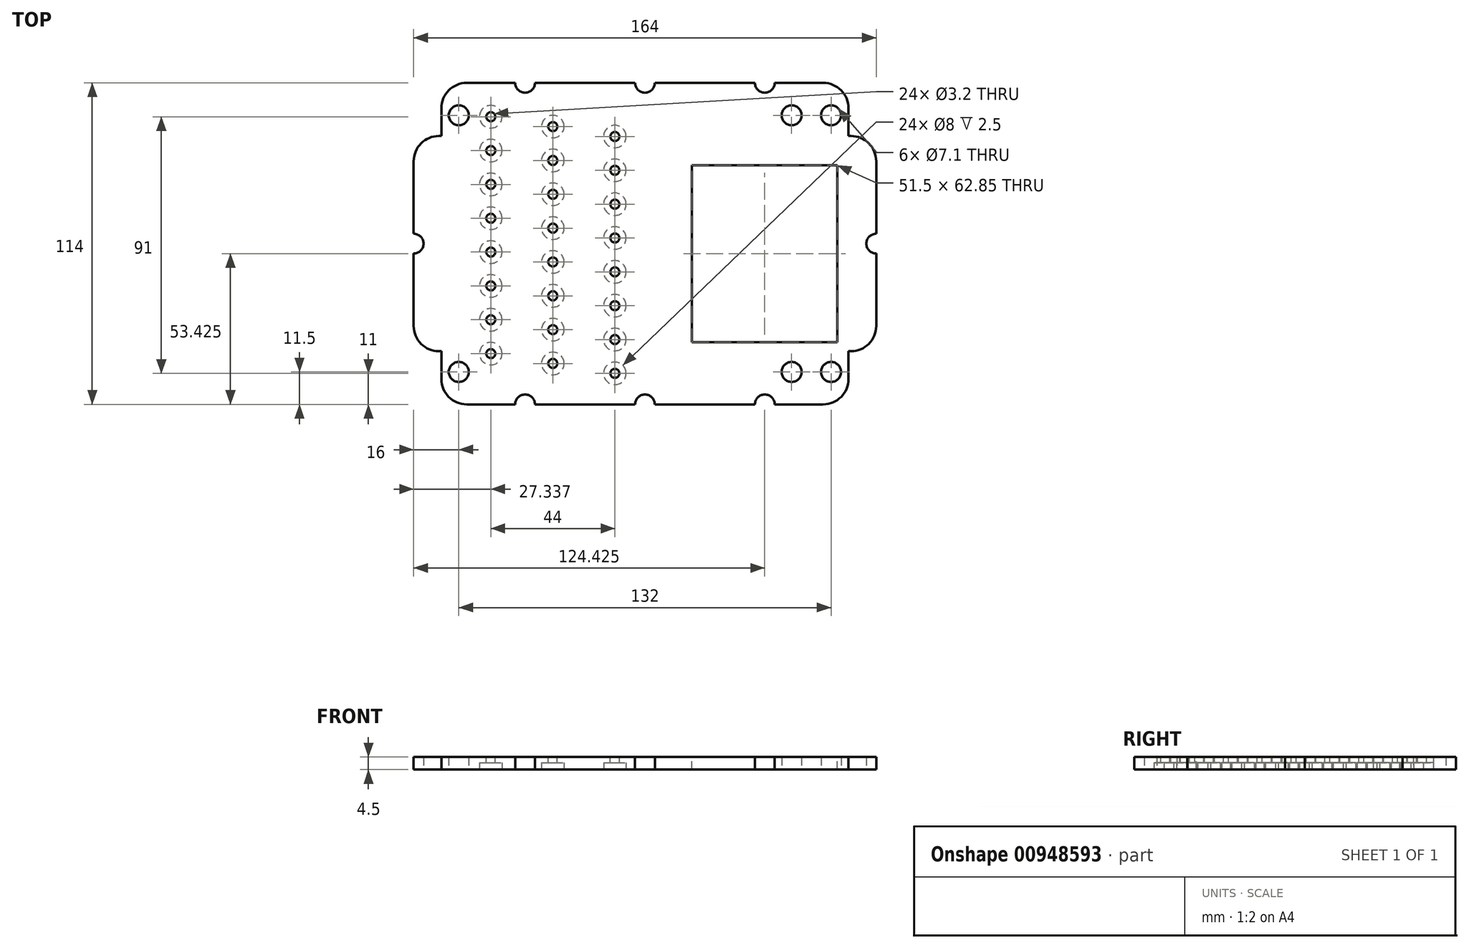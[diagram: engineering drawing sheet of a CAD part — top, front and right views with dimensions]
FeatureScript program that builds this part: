
annotation { "Feature Type Name" : "Feature", "Feature Type Description" : "" }
export const myFeature = defineFeature(function(context is Context, id is Id, definition is map)
    precondition{}
    {
        {
            var Q0;
            Q0=qCreatedBy(makeId("Top.planeOp"),FACE);
            var sketch = newSketch(context, id + "F0", { "sketchPlane" : qUnion([Q0])});
            skLineSegment(sketch, "E0", {"start": v(-63.17, -57) * mm, "end": v(-46, -57) * mm});
            skLineSegment(sketch, "E1", {"start": v(0, -57) * mm, "end": v(0, 57) * mm, "construction": true});
            skLineSegment(sketch, "E2", {"start": v(-82, 0) * mm, "end": v(82, 0) * mm, "construction": true});
            skLineSegment(sketch, "E3", {"start": v(82, -29.18) * mm, "end": v(82, -3.5) * mm});
            skLineSegment(sketch, "E4", {"start": v(72.18, -48) * mm, "end": v(72.18, -38.17) * mm});
            skLineSegment(sketch, "E5", {"start": v(72.18, -38.17) * mm, "end": v(73, -38.17) * mm});
            skLineSegment(sketch, "E6.MirrorCS", {"start": v(-82, -29.18) * mm, "end": v(-82, -3.5) * mm});
            skLineSegment(sketch, "E7.MirrorCS", {"start": v(-72.18, -48) * mm, "end": v(-72.18, -38.17) * mm});
            skLineSegment(sketch, "E8.MirrorCS", {"start": v(-72.18, -38.17) * mm, "end": v(-73, -38.17) * mm});
            skLineSegment(sketch, "E9.MirrorCS", {"start": v(72.18, 38.17) * mm, "end": v(73, 38.17) * mm});
            skLineSegment(sketch, "E10.MirrorCS", {"start": v(72.18, 48) * mm, "end": v(72.18, 38.17) * mm});
            skLineSegment(sketch, "E11.MirrorCS", {"start": v(-72.18, 38.17) * mm, "end": v(-73, 38.17) * mm});
            skLineSegment(sketch, "E12.MirrorCS", {"start": v(-63.17, 57) * mm, "end": v(-46, 57) * mm});
            skLineSegment(sketch, "E13.MirrorCS", {"start": v(-72.18, 48) * mm, "end": v(-72.18, 38.17) * mm});
            skCircle(sketch, "E14", {"center": v(66, 45.5) * mm, "radius": 3.55 * mm});
            skPoint(sketch, "E15", {"position": v(0, 45.5) * mm});
            skLineSegment(sketch, "E16", {"start": v(66, 45.5) * mm, "end": v(-66, 45.5) * mm, "construction": true});
            skCircle(sketch, "E17.MirrorC", {"center": v(-66, 45.5) * mm, "radius": 3.55 * mm});
            skCircle(sketch, "E18", {"center": v(52, 45.5) * mm, "radius": 3.55 * mm});
            skCircle(sketch, "E19.MirrorC", {"center": v(66, -45.5) * mm, "radius": 3.55 * mm});
            skCircle(sketch, "E20.MirrorC", {"center": v(52, -45.5) * mm, "radius": 3.55 * mm});
            skCircle(sketch, "E21.MirrorC", {"center": v(-66, -45.5) * mm, "radius": 3.55 * mm});
            skArc(sketch, "E22", {"start": v(82, -3.5) * mm, "mid": v(78.5, 0) * mm, "end": v(82, 3.5) * mm});
            skArc(sketch, "E23.MirrorCS", {"start": v(-82, -3.5) * mm, "mid": v(-78.5, 0) * mm, "end": v(-82, 3.5) * mm});
            skLineSegment(sketch, "E24.trimOffspring", {"start": v(82, 3.5) * mm, "end": v(82, 29.18) * mm});
            skLineSegment(sketch, "E25.trimOffspring", {"start": v(-82, 3.5) * mm, "end": v(-82, 29.18) * mm});
            skArc(sketch, "E26", {"start": v(-3.5, 57) * mm, "mid": v(0, 53.5) * mm, "end": v(3.5, 57) * mm});
            skArc(sketch, "E27", {"start": v(-46, 57) * mm, "mid": v(-42.5, 53.5) * mm, "end": v(-39, 57) * mm});
            skArc(sketch, "E28.MirrorCS", {"start": v(46, 57) * mm, "mid": v(42.5, 53.5) * mm, "end": v(39, 57) * mm});
            skLineSegment(sketch, "E29.trimOffspring", {"start": v(-39, 57) * mm, "end": v(-3.5, 57) * mm});
            skLineSegment(sketch, "E30.trimOffspring", {"start": v(3.5, 57) * mm, "end": v(39, 57) * mm});
            skLineSegment(sketch, "E31.trimOffspring", {"start": v(46, 57) * mm, "end": v(63.17, 57) * mm});
            skArc(sketch, "E32.MirrorCS", {"start": v(46, -57) * mm, "mid": v(42.5, -53.5) * mm, "end": v(39, -57) * mm});
            skArc(sketch, "E33.MirrorCS", {"start": v(-3.5, -57) * mm, "mid": v(0, -53.5) * mm, "end": v(3.5, -57) * mm});
            skArc(sketch, "E34.MirrorCS", {"start": v(-46, -57) * mm, "mid": v(-42.5, -53.5) * mm, "end": v(-39, -57) * mm});
            skLineSegment(sketch, "E35.trimOffspring", {"start": v(-39, -57) * mm, "end": v(-3.5, -57) * mm});
            skLineSegment(sketch, "E36.trimOffspring", {"start": v(3.5, -57) * mm, "end": v(39, -57) * mm});
            skLineSegment(sketch, "E37.trimOffspring", {"start": v(46, -57) * mm, "end": v(63.17, -57) * mm});
            skPoint(sketch, "E38.visualSharp", {"position": v(-82, 38.17) * mm});
            skArc(sketch, "E38.filletArc", {"start": v(-73, 38.18) * mm, "mid": v(-79.36, 35.54) * mm, "end": v(-82, 29.18) * mm});
            skPoint(sketch, "E39.visualSharp", {"position": v(-72.17, 57) * mm});
            skArc(sketch, "E39.filletArc", {"start": v(-63.17, 57) * mm, "mid": v(-69.54, 54.36) * mm, "end": v(-72.17, 48) * mm});
            skPoint(sketch, "E40.visualSharp", {"position": v(-82, -38.17) * mm});
            skArc(sketch, "E40.filletArc", {"start": v(-82, -29.18) * mm, "mid": v(-79.36, -35.54) * mm, "end": v(-73, -38.18) * mm});
            skPoint(sketch, "E41.visualSharp", {"position": v(-72.17, -57) * mm});
            skArc(sketch, "E41.filletArc", {"start": v(-72.17, -48) * mm, "mid": v(-69.54, -54.36) * mm, "end": v(-63.17, -57) * mm});
            skPoint(sketch, "E42.visualSharp", {"position": v(72.18, -57) * mm});
            skArc(sketch, "E42.filletArc", {"start": v(63.17, -57) * mm, "mid": v(69.54, -54.36) * mm, "end": v(72.17, -48) * mm});
            skPoint(sketch, "E43.visualSharp", {"position": v(82, -38.17) * mm});
            skArc(sketch, "E43.filletArc", {"start": v(73, -38.18) * mm, "mid": v(79.36, -35.54) * mm, "end": v(82, -29.18) * mm});
            skPoint(sketch, "E44.visualSharp", {"position": v(82, 38.17) * mm});
            skArc(sketch, "E44.filletArc", {"start": v(82, 29.18) * mm, "mid": v(79.36, 35.54) * mm, "end": v(73, 38.18) * mm});
            skPoint(sketch, "E45.visualSharp", {"position": v(72.18, 57) * mm});
            skArc(sketch, "E45.filletArc", {"start": v(72.17, 48) * mm, "mid": v(69.54, 54.36) * mm, "end": v(63.17, 57) * mm});
            skSolve(sketch);
        }
        {
            var Q0;
            Q0 = qSketchRegion(id + "F0", true);
            extrude(context, id + "F1", {"entities" : qUnion([Q0]), "depth" : 4.5 * mm, "offsetDistance" : 25 * mm});
        }
        {
            var Q0;
            Q0=makeQuery(id+"F1.opExtrude","CAP_FACE",FACE,{"disambiguationData":[OSD([sQuery(id+"F0.wireOp",EDGE,"E0"),sQuery(id+"F0.wireOp",EDGE,"E3"),sQuery(id+"F0.wireOp",EDGE,"E4"),sQuery(id+"F0.wireOp",EDGE,"E5"),sQuery(id+"F0.wireOp",EDGE,"E6.MirrorCS"),sQuery(id+"F0.wireOp",EDGE,"E7.MirrorCS"),sQuery(id+"F0.wireOp",EDGE,"E8.MirrorCS"),sQuery(id+"F0.wireOp",EDGE,"E9.MirrorCS"),sQuery(id+"F0.wireOp",EDGE,"E10.MirrorCS"),sQuery(id+"F0.wireOp",EDGE,"E11.MirrorCS"),sQuery(id+"F0.wireOp",EDGE,"E12.MirrorCS"),sQuery(id+"F0.wireOp",EDGE,"E13.MirrorCS"),sQuery(id+"F0.wireOp",EDGE,"E14"),sQuery(id+"F0.wireOp",EDGE,"E17.MirrorC"),sQuery(id+"F0.wireOp",EDGE,"E18"),sQuery(id+"F0.wireOp",EDGE,"E19.MirrorC"),sQuery(id+"F0.wireOp",EDGE,"E20.MirrorC"),sQuery(id+"F0.wireOp",EDGE,"E21.MirrorC"),sQuery(id+"F0.wireOp",EDGE,"E22"),sQuery(id+"F0.wireOp",EDGE,"E23.MirrorCS"),sQuery(id+"F0.wireOp",EDGE,"E24.trimOffspring"),sQuery(id+"F0.wireOp",EDGE,"E25.trimOffspring"),sQuery(id+"F0.wireOp",EDGE,"E26"),sQuery(id+"F0.wireOp",EDGE,"E27"),sQuery(id+"F0.wireOp",EDGE,"E28.MirrorCS"),sQuery(id+"F0.wireOp",EDGE,"E29.trimOffspring"),sQuery(id+"F0.wireOp",EDGE,"E30.trimOffspring"),sQuery(id+"F0.wireOp",EDGE,"E31.trimOffspring"),sQuery(id+"F0.wireOp",EDGE,"E32.MirrorCS"),sQuery(id+"F0.wireOp",EDGE,"E33.MirrorCS"),sQuery(id+"F0.wireOp",EDGE,"E34.MirrorCS"),sQuery(id+"F0.wireOp",EDGE,"E35.trimOffspring"),sQuery(id+"F0.wireOp",EDGE,"E36.trimOffspring"),sQuery(id+"F0.wireOp",EDGE,"E37.trimOffspring")])],"isStart":false});
            var sketch = newSketch(context, id + "F2", { "sketchPlane" : qUnion([Q0])});
            skLineSegment(sketch, "E46.bottom", {"start": v(16.68, 27.85) * mm, "end": v(68.18, 27.85) * mm});
            skLineSegment(sketch, "E46.top", {"start": v(16.68, -35) * mm, "end": v(68.18, -35) * mm});
            skLineSegment(sketch, "E46.left", {"start": v(16.68, 27.85) * mm, "end": v(16.68, -35) * mm});
            skLineSegment(sketch, "E46.right", {"start": v(68.18, 27.85) * mm, "end": v(68.18, -35) * mm});
            skLineSegment(sketch, "E47", {"start": v(68.18, -35) * mm, "end": v(68.18, 35) * mm, "construction": true});
            skLineSegment(sketch, "E48", {"start": v(-78.5, 0) * mm, "end": v(78.5, 0) * mm, "construction": true});
            skPoint(sketch, "E49", {"position": v(68.18, 0) * mm});
            skSolve(sketch);
        }
        {
            var Q0;
            Q0 = qSketchRegion(id + "F2", true);
            extrude(context, id + "F3", {"entities" : qUnion([Q0]), "operationType" : NewBodyOperationType.REMOVE, "endBound" : BoundingType.THROUGH_ALL, "oppositeDirection" : true, "depth" : 25 * mm, "offsetDistance" : 25 * mm});
        }
        {
            var Q0;
            Q0=makeQuery(id+"F1.opExtrude","CAP_FACE",FACE,{"disambiguationData":[OSD([sQuery(id+"F0.wireOp",EDGE,"E0"),sQuery(id+"F0.wireOp",EDGE,"E3"),sQuery(id+"F0.wireOp",EDGE,"E4"),sQuery(id+"F0.wireOp",EDGE,"E5"),sQuery(id+"F0.wireOp",EDGE,"E6.MirrorCS"),sQuery(id+"F0.wireOp",EDGE,"E7.MirrorCS"),sQuery(id+"F0.wireOp",EDGE,"E8.MirrorCS"),sQuery(id+"F0.wireOp",EDGE,"E9.MirrorCS"),sQuery(id+"F0.wireOp",EDGE,"E10.MirrorCS"),sQuery(id+"F0.wireOp",EDGE,"E11.MirrorCS"),sQuery(id+"F0.wireOp",EDGE,"E12.MirrorCS"),sQuery(id+"F0.wireOp",EDGE,"E13.MirrorCS"),sQuery(id+"F0.wireOp",EDGE,"E14"),sQuery(id+"F0.wireOp",EDGE,"E17.MirrorC"),sQuery(id+"F0.wireOp",EDGE,"E18"),sQuery(id+"F0.wireOp",EDGE,"E19.MirrorC"),sQuery(id+"F0.wireOp",EDGE,"E20.MirrorC"),sQuery(id+"F0.wireOp",EDGE,"E21.MirrorC"),sQuery(id+"F0.wireOp",EDGE,"E22"),sQuery(id+"F0.wireOp",EDGE,"E23.MirrorCS"),sQuery(id+"F0.wireOp",EDGE,"E24.trimOffspring"),sQuery(id+"F0.wireOp",EDGE,"E25.trimOffspring"),sQuery(id+"F0.wireOp",EDGE,"E26"),sQuery(id+"F0.wireOp",EDGE,"E27"),sQuery(id+"F0.wireOp",EDGE,"E28.MirrorCS"),sQuery(id+"F0.wireOp",EDGE,"E29.trimOffspring"),sQuery(id+"F0.wireOp",EDGE,"E30.trimOffspring"),sQuery(id+"F0.wireOp",EDGE,"E31.trimOffspring"),sQuery(id+"F0.wireOp",EDGE,"E32.MirrorCS"),sQuery(id+"F0.wireOp",EDGE,"E33.MirrorCS"),sQuery(id+"F0.wireOp",EDGE,"E34.MirrorCS"),sQuery(id+"F0.wireOp",EDGE,"E35.trimOffspring"),sQuery(id+"F0.wireOp",EDGE,"E36.trimOffspring"),sQuery(id+"F0.wireOp",EDGE,"E37.trimOffspring")])],"isStart":false});
            var sketch = newSketch(context, id + "F4", { "sketchPlane" : qUnion([Q0])});
            skLineSegment(sketch, "E50.bottom", {"start": v(-66.66, 29.11) * mm, "end": v(-42.66, 29.11) * mm, "construction": true});
            skLineSegment(sketch, "E50.top", {"start": v(-66.66, -30.89) * mm, "end": v(-42.66, -30.89) * mm, "construction": true});
            skLineSegment(sketch, "E50.left", {"start": v(-66.66, 29.11) * mm, "end": v(-66.66, -30.89) * mm, "construction": true});
            skLineSegment(sketch, "E50.right", {"start": v(-42.66, 29.11) * mm, "end": v(-42.66, -30.89) * mm, "construction": true});
            skLineSegment(sketch, "E51", {"start": v(-32.66, -51.43) * mm, "end": v(-32.66, 49.38) * mm, "construction": true});
            skLineSegment(sketch, "E52.MirrorCS", {"start": v(1.34, -30.89) * mm, "end": v(-22.66, -30.89) * mm, "construction": true});
            skLineSegment(sketch, "E53.MirrorCS", {"start": v(-22.66, 29.11) * mm, "end": v(-22.66, -30.89) * mm, "construction": true});
            skLineSegment(sketch, "E54.MirrorCS", {"start": v(1.34, 29.11) * mm, "end": v(1.34, -30.89) * mm, "construction": true});
            skLineSegment(sketch, "E55.MirrorCS", {"start": v(1.34, 29.11) * mm, "end": v(-22.66, 29.11) * mm, "construction": true});
            skLineSegment(sketch, "E56", {"start": v(-82, 16.34) * mm, "end": v(-66.66, 16.34) * mm, "construction": true});
            skLineSegment(sketch, "E57", {"start": v(1.34, 16.34) * mm, "end": v(16.67, 16.34) * mm, "construction": true});
            skLineSegment(sketch, "E58", {"start": v(-54.66, 29.11) * mm, "end": v(-54.66, -30.89) * mm, "construction": true});
            skLineSegment(sketch, "E59", {"start": v(-54.66, 29.11) * mm, "end": v(-54.66, 57) * mm, "construction": true});
            skCircle(sketch, "E60", {"center": v(-54.66, 45) * mm, "radius": 1.6 * mm});
            skCircle(sketch, "E61.1.0.0", {"center": v(-54.66, 33) * mm, "radius": 1.6 * mm});
            skCircle(sketch, "E61.2.0.0", {"center": v(-54.66, 21) * mm, "radius": 1.6 * mm});
            skCircle(sketch, "E61.3.0.0", {"center": v(-54.66, 9) * mm, "radius": 1.6 * mm});
            skCircle(sketch, "E61.4.0.0", {"center": v(-54.66, -3) * mm, "radius": 1.6 * mm});
            skCircle(sketch, "E61.5.0.0", {"center": v(-54.66, -15) * mm, "radius": 1.6 * mm});
            skCircle(sketch, "E61.6.0.0", {"center": v(-54.66, -27) * mm, "radius": 1.6 * mm});
            skCircle(sketch, "E61.7.0.0", {"center": v(-54.66, -39) * mm, "radius": 1.6 * mm});
            skLineSegment(sketch, "E61.direction1", {"start": v(-54.66, 45) * mm, "end": v(-54.66, 33) * mm, "construction": true});
            skLineSegment(sketch, "E62", {"start": v(-10.66, 29.11) * mm, "end": v(-10.66, 57) * mm, "construction": true});
            skCircle(sketch, "E63", {"center": v(-10.66, 38) * mm, "radius": 1.6 * mm});
            skLineSegment(sketch, "E64", {"start": v(-10.66, 29.11) * mm, "end": v(-10.66, -30.89) * mm, "construction": true});
            skCircle(sketch, "E65.1.0.0", {"center": v(-10.66, 26) * mm, "radius": 1.6 * mm});
            skCircle(sketch, "E65.2.0.0", {"center": v(-10.66, 14) * mm, "radius": 1.6 * mm});
            skCircle(sketch, "E65.3.0.0", {"center": v(-10.66, 2) * mm, "radius": 1.6 * mm});
            skCircle(sketch, "E65.4.0.0", {"center": v(-10.66, -10) * mm, "radius": 1.6 * mm});
            skCircle(sketch, "E65.5.0.0", {"center": v(-10.66, -22) * mm, "radius": 1.6 * mm});
            skCircle(sketch, "E65.6.0.0", {"center": v(-10.66, -34) * mm, "radius": 1.6 * mm});
            skCircle(sketch, "E65.7.0.0", {"center": v(-10.66, -46) * mm, "radius": 1.6 * mm});
            skLineSegment(sketch, "E65.direction1", {"start": v(-10.66, 38) * mm, "end": v(-10.66, 26) * mm, "construction": true});
            skCircle(sketch, "E66", {"center": v(-32.66, 41.5) * mm, "radius": 1.6 * mm});
            skLineSegment(sketch, "E67", {"start": v(-54.66, 45) * mm, "end": v(-10.66, 38) * mm, "construction": true});
            skCircle(sketch, "E68.1.0.0", {"center": v(-32.66, 29.5) * mm, "radius": 1.6 * mm});
            skCircle(sketch, "E68.2.0.0", {"center": v(-32.66, 17.5) * mm, "radius": 1.6 * mm});
            skCircle(sketch, "E68.3.0.0", {"center": v(-32.66, 5.5) * mm, "radius": 1.6 * mm});
            skCircle(sketch, "E68.4.0.0", {"center": v(-32.66, -6.5) * mm, "radius": 1.6 * mm});
            skCircle(sketch, "E68.5.0.0", {"center": v(-32.66, -18.5) * mm, "radius": 1.6 * mm});
            skCircle(sketch, "E68.6.0.0", {"center": v(-32.66, -30.5) * mm, "radius": 1.6 * mm});
            skCircle(sketch, "E68.7.0.0", {"center": v(-32.66, -42.5) * mm, "radius": 1.6 * mm});
            skLineSegment(sketch, "E68.direction1", {"start": v(-32.66, 41.5) * mm, "end": v(-32.66, 29.5) * mm, "construction": true});
            skSolve(sketch);
        }
        {
            var Q0;
            Q0 = qSketchRegion(id + "F4", true);
            extrude(context, id + "F5", {"entities" : qUnion([Q0]), "operationType" : NewBodyOperationType.REMOVE, "endBound" : BoundingType.THROUGH_ALL, "oppositeDirection" : true, "depth" : 25 * mm, "offsetDistance" : 25 * mm});
        }
        {
            var Q0;
            Q0=makeQuery(id+"F1.opExtrude","CAP_FACE",FACE,{"disambiguationData":[OSD([sQuery(id+"F0.wireOp",EDGE,"E0"),sQuery(id+"F0.wireOp",EDGE,"E3"),sQuery(id+"F0.wireOp",EDGE,"E4"),sQuery(id+"F0.wireOp",EDGE,"E5"),sQuery(id+"F0.wireOp",EDGE,"E6.MirrorCS"),sQuery(id+"F0.wireOp",EDGE,"E7.MirrorCS"),sQuery(id+"F0.wireOp",EDGE,"E8.MirrorCS"),sQuery(id+"F0.wireOp",EDGE,"E9.MirrorCS"),sQuery(id+"F0.wireOp",EDGE,"E10.MirrorCS"),sQuery(id+"F0.wireOp",EDGE,"E11.MirrorCS"),sQuery(id+"F0.wireOp",EDGE,"E12.MirrorCS"),sQuery(id+"F0.wireOp",EDGE,"E13.MirrorCS"),sQuery(id+"F0.wireOp",EDGE,"E14"),sQuery(id+"F0.wireOp",EDGE,"E17.MirrorC"),sQuery(id+"F0.wireOp",EDGE,"E18"),sQuery(id+"F0.wireOp",EDGE,"E19.MirrorC"),sQuery(id+"F0.wireOp",EDGE,"E20.MirrorC"),sQuery(id+"F0.wireOp",EDGE,"E21.MirrorC"),sQuery(id+"F0.wireOp",EDGE,"E22"),sQuery(id+"F0.wireOp",EDGE,"E23.MirrorCS"),sQuery(id+"F0.wireOp",EDGE,"E24.trimOffspring"),sQuery(id+"F0.wireOp",EDGE,"E25.trimOffspring"),sQuery(id+"F0.wireOp",EDGE,"E26"),sQuery(id+"F0.wireOp",EDGE,"E27"),sQuery(id+"F0.wireOp",EDGE,"E28.MirrorCS"),sQuery(id+"F0.wireOp",EDGE,"E29.trimOffspring"),sQuery(id+"F0.wireOp",EDGE,"E30.trimOffspring"),sQuery(id+"F0.wireOp",EDGE,"E31.trimOffspring"),sQuery(id+"F0.wireOp",EDGE,"E32.MirrorCS"),sQuery(id+"F0.wireOp",EDGE,"E33.MirrorCS"),sQuery(id+"F0.wireOp",EDGE,"E34.MirrorCS"),sQuery(id+"F0.wireOp",EDGE,"E35.trimOffspring"),sQuery(id+"F0.wireOp",EDGE,"E36.trimOffspring"),sQuery(id+"F0.wireOp",EDGE,"E37.trimOffspring")])],"isStart":true});
            var sketch = newSketch(context, id + "F6", { "sketchPlane" : qUnion([Q0])});
            skCircle(sketch, "E69", {"center": v(-10.66, 46) * mm, "radius": 4 * mm});
            skCircle(sketch, "E70", {"center": v(-10.66, 34) * mm, "radius": 4 * mm});
            skCircle(sketch, "E71", {"center": v(-10.66, 22) * mm, "radius": 4 * mm});
            skCircle(sketch, "E72", {"center": v(-10.66, 10) * mm, "radius": 4 * mm});
            skCircle(sketch, "E73", {"center": v(-10.66, -2) * mm, "radius": 4 * mm});
            skCircle(sketch, "E74", {"center": v(-10.66, -14) * mm, "radius": 4 * mm});
            skCircle(sketch, "E75", {"center": v(-10.66, -26) * mm, "radius": 4 * mm});
            skCircle(sketch, "E76", {"center": v(-54.66, 39) * mm, "radius": 4 * mm});
            skCircle(sketch, "E77", {"center": v(-54.66, 27) * mm, "radius": 4 * mm});
            skCircle(sketch, "E78", {"center": v(-54.66, 15) * mm, "radius": 4 * mm});
            skCircle(sketch, "E79", {"center": v(-54.66, 3) * mm, "radius": 4 * mm});
            skCircle(sketch, "E80", {"center": v(-54.66, -9) * mm, "radius": 4 * mm});
            skCircle(sketch, "E81", {"center": v(-54.66, -21) * mm, "radius": 4 * mm});
            skCircle(sketch, "E82", {"center": v(-54.66, -33) * mm, "radius": 4 * mm});
            skCircle(sketch, "E83", {"center": v(-10.66, -38) * mm, "radius": 4 * mm});
            skCircle(sketch, "E84", {"center": v(-54.66, -45) * mm, "radius": 4 * mm});
            skCircle(sketch, "E85", {"center": v(-32.66, 42.5) * mm, "radius": 4 * mm});
            skCircle(sketch, "E86", {"center": v(-32.66, 30.5) * mm, "radius": 4 * mm});
            skCircle(sketch, "E87", {"center": v(-32.66, 18.5) * mm, "radius": 4 * mm});
            skCircle(sketch, "E88", {"center": v(-32.66, 6.5) * mm, "radius": 4 * mm});
            skCircle(sketch, "E89", {"center": v(-32.66, -5.5) * mm, "radius": 4 * mm});
            skCircle(sketch, "E90", {"center": v(-32.66, -17.5) * mm, "radius": 4 * mm});
            skCircle(sketch, "E91", {"center": v(-32.66, -29.5) * mm, "radius": 4 * mm});
            skCircle(sketch, "E92", {"center": v(-32.66, -41.5) * mm, "radius": 4 * mm});
            skSolve(sketch);
        }
        {
            var Q0;
            Q0 = qSketchRegion(id + "F6", true);
            extrude(context, id + "F7", {"entities" : qUnion([Q0]), "operationType" : NewBodyOperationType.REMOVE, "oppositeDirection" : true, "depth" : 2.5 * mm, "offsetDistance" : 25 * mm});
        }
    });
